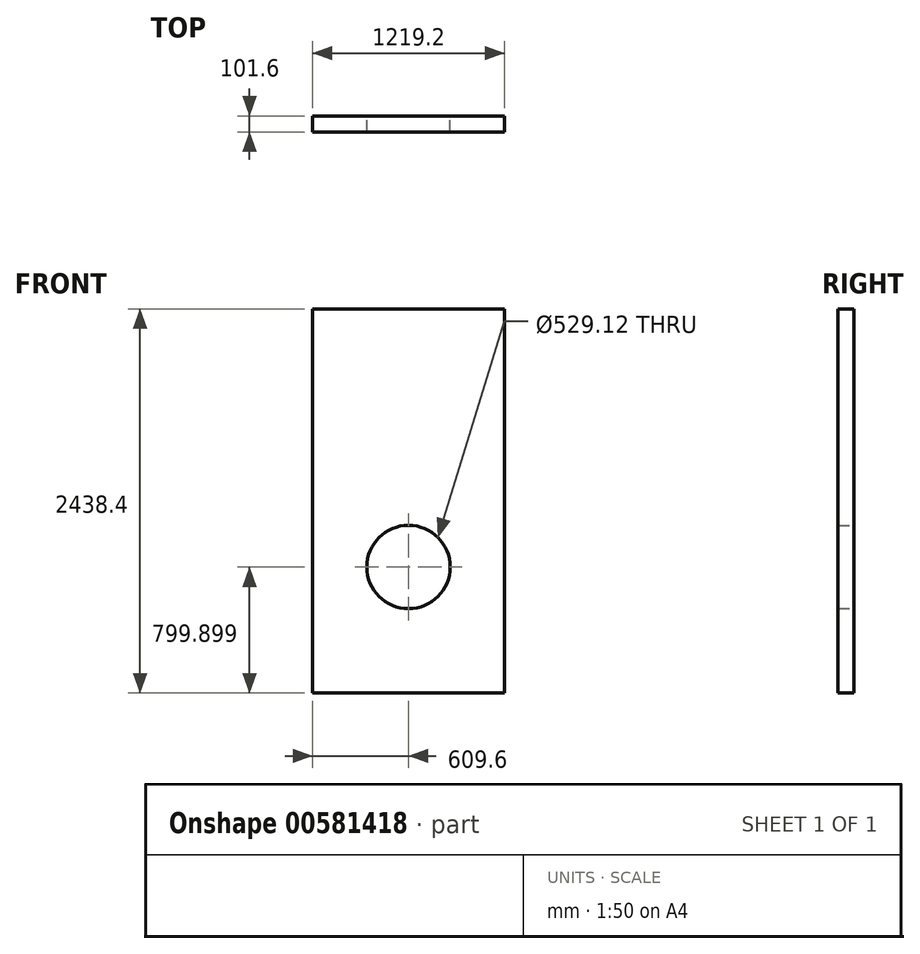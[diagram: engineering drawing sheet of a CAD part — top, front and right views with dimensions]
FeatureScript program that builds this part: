
annotation { "Feature Type Name" : "Feature", "Feature Type Description" : "" }
export const myFeature = defineFeature(function(context is Context, id is Id, definition is map)
    precondition{}
    {
        {
            var Q0;
            Q0=qCreatedBy(makeId("Front.planeOp"),FACE);
            var sketch = newSketch(context, id + "F0", { "sketchPlane" : qUnion([Q0])});
            skLineSegment(sketch, "E0.bottom", {"start": v(609.6, -1219.2) * mm, "end": v(-609.6, -1219.2) * mm});
            skLineSegment(sketch, "E0.top", {"start": v(609.6, 1219.2) * mm, "end": v(-609.6, 1219.2) * mm});
            skLineSegment(sketch, "E0.left", {"start": v(609.6, -1219.2) * mm, "end": v(609.6, 1219.2) * mm});
            skLineSegment(sketch, "E0.right", {"start": v(-609.6, -1219.2) * mm, "end": v(-609.6, 1219.2) * mm});
            skPoint(sketch, "E0.middle", {"position": v(0, 0) * mm});
            skSolve(sketch);
        }
        {
            var Q0;
            Q0 = qSketchRegion(id + "F0", true);
            extrude(context, id + "F1", {"entities" : qUnion([Q0]), "depth" : 101.6 * mm, "offsetDistance" : 25.4 * mm});
        }
        {
            var Q0;
            Q0=makeQuery(id+"F1.opExtrude","CAP_FACE",FACE,{"disambiguationData":[OSD([sQuery(id+"F0.wireOp",EDGE,"E0.bottom"),sQuery(id+"F0.wireOp",EDGE,"E0.top"),sQuery(id+"F0.wireOp",EDGE,"E0.left"),sQuery(id+"F0.wireOp",EDGE,"E0.right")])],"isStart":true});
            var sketch = newSketch(context, id + "F2", { "sketchPlane" : qUnion([Q0])});
            skCircle(sketch, "E1", {"center": v(0, -419.3) * mm, "radius": 264.56 * mm});
            skSolve(sketch);
        }
        {
            var Q0;
            Q0 = qSketchRegion(id + "F2", true);
            extrude(context, id + "F3", {"entities" : qUnion([Q0]), "operationType" : NewBodyOperationType.REMOVE, "endBound" : BoundingType.THROUGH_ALL, "oppositeDirection" : true, "depth" : 25.4 * mm, "offsetDistance" : 25.4 * mm});
        }
    });
